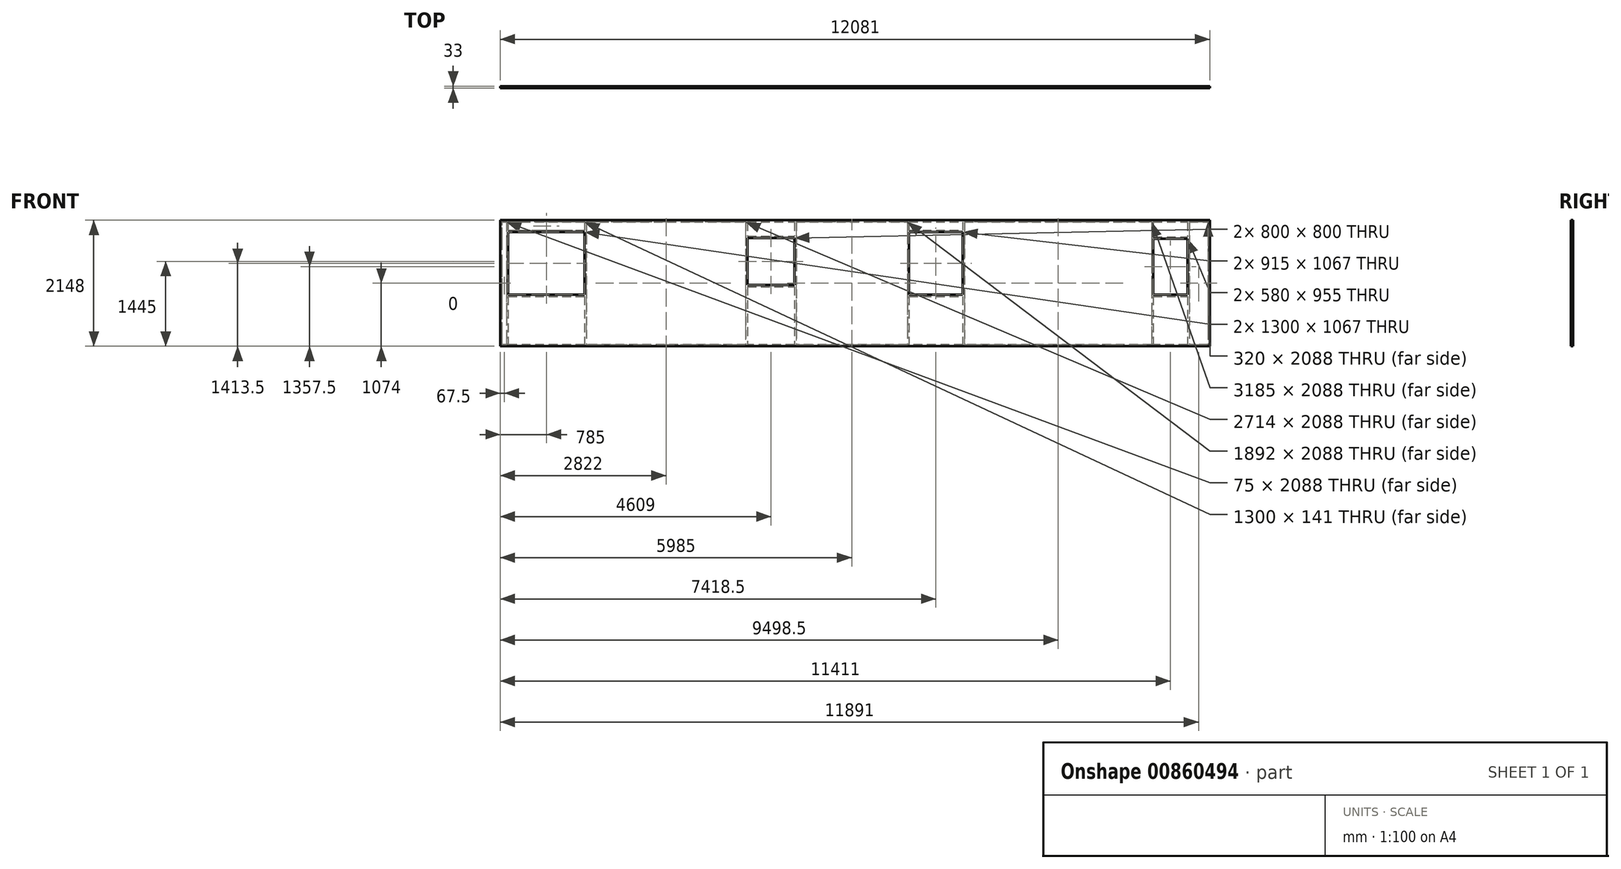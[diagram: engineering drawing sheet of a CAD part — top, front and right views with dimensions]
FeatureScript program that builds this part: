
annotation { "Feature Type Name" : "Feature", "Feature Type Description" : "" }
export const myFeature = defineFeature(function(context is Context, id is Id, definition is map)
    precondition{}
    {
        {
            var Q0;
            Q0=qCreatedBy(makeId("Front.planeOp"),FACE);
            var sketch = newSketch(context, id + "F0", { "sketchPlane" : qUnion([Q0])});
            skLineSegment(sketch, "E0", {"start": v(0, 0) * mm, "end": v(-6025.5, 0) * mm});
            skLineSegment(sketch, "E1", {"start": v(-6025.5, 0) * mm, "end": v(-6025.5, 2088) * mm});
            skLineSegment(sketch, "E2", {"start": v(-6025.5, 2088) * mm, "end": v(6025.5, 2088) * mm});
            skLineSegment(sketch, "E3", {"start": v(6025.5, 2088) * mm, "end": v(6025.5, 0) * mm});
            skLineSegment(sketch, "E4", {"start": v(6025.5, 0) * mm, "end": v(0, 0) * mm});
            skLineSegment(sketch, "E5", {"start": v(5995.5, 2088) * mm, "end": v(5995.5, 0) * mm});
            skLineSegment(sketch, "E6", {"start": v(6025.5, 2118) * mm, "end": v(1575.5, 2118) * mm});
            skLineSegment(sketch, "E7", {"start": v(6025.5, 2118) * mm, "end": v(6025.5, 2088) * mm});
            skLineSegment(sketch, "E8", {"start": v(1575.5, 2118) * mm, "end": v(1575.5, 2088) * mm});
            skLineSegment(sketch, "E9", {"start": v(1575.5, 2118) * mm, "end": v(-3474.5, 2118) * mm});
            skLineSegment(sketch, "E10", {"start": v(-3474.5, 2118) * mm, "end": v(-3474.5, 2088) * mm});
            skLineSegment(sketch, "E11", {"start": v(-3474.5, 2118) * mm, "end": v(-6055.5, 2118) * mm});
            skLineSegment(sketch, "E12", {"start": v(-6055.5, 2118) * mm, "end": v(-6055.5, -30) * mm});
            skLineSegment(sketch, "E13", {"start": v(-6055.5, -30) * mm, "end": v(6025.5, -30) * mm});
            skLineSegment(sketch, "E14", {"start": v(6025.5, -30) * mm, "end": v(6025.5, 0) * mm});
            skLineSegment(sketch, "E15", {"start": v(5675.5, 2088) * mm, "end": v(5675.5, 0) * mm});
            skLineSegment(sketch, "E16", {"start": v(5065.5, 2088) * mm, "end": v(5065.5, 0) * mm});
            skLineSegment(sketch, "E17", {"start": v(5645.5, 2088) * mm, "end": v(5645.5, 0) * mm});
            skLineSegment(sketch, "E18", {"start": v(5035.5, 2088) * mm, "end": v(5035.5, 0) * mm});
            skLineSegment(sketch, "E19", {"start": v(5065.5, 850) * mm, "end": v(5645.5, 850) * mm});
            skLineSegment(sketch, "E20", {"start": v(5065.5, 820) * mm, "end": v(5645.5, 820) * mm});
            skLineSegment(sketch, "E21", {"start": v(5065.5, 1805) * mm, "end": v(5645.5, 1805) * mm});
            skLineSegment(sketch, "E22", {"start": v(5065.5, 1835) * mm, "end": v(5645.5, 1835) * mm});
            skLineSegment(sketch, "E23", {"start": v(1850.5, 2088) * mm, "end": v(1850.5, 0) * mm});
            skLineSegment(sketch, "E24", {"start": v(1820.5, 2088) * mm, "end": v(1820.5, 0) * mm});
            skLineSegment(sketch, "E25", {"start": v(875.5, 2088) * mm, "end": v(875.5, 0) * mm});
            skLineSegment(sketch, "E26", {"start": v(905.5, 2088) * mm, "end": v(905.5, 0) * mm});
            skLineSegment(sketch, "E27", {"start": v(905.5, 850) * mm, "end": v(1820.5, 850) * mm});
            skLineSegment(sketch, "E28", {"start": v(905.5, 820) * mm, "end": v(1820.5, 820) * mm});
            skLineSegment(sketch, "E29", {"start": v(905.5, 1947) * mm, "end": v(1820.5, 1947) * mm});
            skLineSegment(sketch, "E30", {"start": v(905.5, 1917) * mm, "end": v(1820.5, 1917) * mm});
            skLineSegment(sketch, "E31", {"start": v(-1016.5, 2088) * mm, "end": v(-1016.5, 0) * mm});
            skLineSegment(sketch, "E32", {"start": v(-1046.5, 2088) * mm, "end": v(-1046.5, 0) * mm});
            skLineSegment(sketch, "E33", {"start": v(-1846.5, 2088) * mm, "end": v(-1846.5, 0) * mm});
            skLineSegment(sketch, "E34", {"start": v(-1876.5, 2088) * mm, "end": v(-1876.5, 0) * mm});
            skLineSegment(sketch, "E35", {"start": v(-1846.5, 1015) * mm, "end": v(-1046.5, 1015) * mm});
            skLineSegment(sketch, "E36", {"start": v(-1846.5, 985) * mm, "end": v(-1046.5, 985) * mm});
            skLineSegment(sketch, "E37", {"start": v(-1846.5, 1845) * mm, "end": v(-1046.5, 1845) * mm});
            skLineSegment(sketch, "E38", {"start": v(-1846.5, 1815) * mm, "end": v(-1046.5, 1815) * mm});
            skLineSegment(sketch, "E39", {"start": v(-5950.5, 2088) * mm, "end": v(-5950.5, 0) * mm});
            skLineSegment(sketch, "E40", {"start": v(-5920.5, 2088) * mm, "end": v(-5920.5, 0) * mm});
            skLineSegment(sketch, "E41", {"start": v(-4620.5, 2088) * mm, "end": v(-4620.5, 0) * mm});
            skLineSegment(sketch, "E42", {"start": v(-4590.5, 2088) * mm, "end": v(-4590.5, 0) * mm});
            skLineSegment(sketch, "E43", {"start": v(-5920.5, 1947) * mm, "end": v(-4620.5, 1947) * mm});
            skLineSegment(sketch, "E44", {"start": v(-5920.5, 1917) * mm, "end": v(-4620.5, 1917) * mm});
            skLineSegment(sketch, "E45", {"start": v(-5920.5, 850) * mm, "end": v(-4620.5, 850) * mm});
            skLineSegment(sketch, "E46", {"start": v(-5920.5, 820) * mm, "end": v(-4620.5, 820) * mm});
            skSolve(sketch);
        }
        {
            var Q0;
            Q0 = qSketchRegion(id + "F0", true);
            var Q1;
            {var subQ0=sQuery(id+"F0.wireOp",EDGE,"E43");Q1=makeQuery(id+"F0.imprint","IMPRINT",FACE,{"disambiguationData":[TD([[makeQuery(id+"F0.imprint","IMPRINT",EDGE,{"derivedFrom":subQ0}),-1.0]])]});}
            var Q2;
            {var subQ5=sQuery(id+"F0.wireOp",EDGE,"E42");Q2=makeQuery(id+"F0.imprint","IMPRINT",FACE,{"disambiguationData":[TD([[makeQuery(id+"F0.imprint","IMPRINT",EDGE,{"derivedFrom":subQ5}),-1.0]])]});}
            var Q3;
            {var subQ0=sQuery(id+"F0.wireOp",EDGE,"E45");Q3=makeQuery(id+"F0.imprint","IMPRINT",FACE,{"disambiguationData":[TD([[makeQuery(id+"F0.imprint","IMPRINT",EDGE,{"derivedFrom":subQ0}),-1.0]])]});}
            var Q4;
            {var subQ4=sQuery(id+"F0.wireOp",EDGE,"E39");Q4=makeQuery(id+"F0.imprint","IMPRINT",FACE,{"disambiguationData":[TD([[makeQuery(id+"F0.imprint","IMPRINT",EDGE,{"derivedFrom":subQ4}),1.0]])]});}
            var Q5;
            {var subQ5=sQuery(id+"F0.wireOp",EDGE,"E34");Q5=makeQuery(id+"F0.imprint","IMPRINT",FACE,{"disambiguationData":[TD([[makeQuery(id+"F0.imprint","IMPRINT",EDGE,{"derivedFrom":subQ5}),1.0]])]});}
            var Q6;
            {var subQ0=sQuery(id+"F0.wireOp",EDGE,"E37");Q6=makeQuery(id+"F0.imprint","IMPRINT",FACE,{"disambiguationData":[TD([[makeQuery(id+"F0.imprint","IMPRINT",EDGE,{"derivedFrom":subQ0}),-1.0]])]});}
            var Q7;
            {var subQ0=sQuery(id+"F0.wireOp",EDGE,"E35");Q7=makeQuery(id+"F0.imprint","IMPRINT",FACE,{"disambiguationData":[TD([[makeQuery(id+"F0.imprint","IMPRINT",EDGE,{"derivedFrom":subQ0}),-1.0]])]});}
            var Q8;
            {var subQ4=sQuery(id+"F0.wireOp",EDGE,"E31");Q8=makeQuery(id+"F0.imprint","IMPRINT",FACE,{"disambiguationData":[TD([[makeQuery(id+"F0.imprint","IMPRINT",EDGE,{"derivedFrom":subQ4}),-1.0]])]});}
            var Q9;
            {var subQ0=sQuery(id+"F0.wireOp",EDGE,"E25");Q9=makeQuery(id+"F0.imprint","IMPRINT",FACE,{"disambiguationData":[TD([[makeQuery(id+"F0.imprint","IMPRINT",EDGE,{"derivedFrom":subQ0}),1.0]])]});}
            var Q10;
            {var subQ0=sQuery(id+"F0.wireOp",EDGE,"E29");Q10=makeQuery(id+"F0.imprint","IMPRINT",FACE,{"disambiguationData":[TD([[makeQuery(id+"F0.imprint","IMPRINT",EDGE,{"derivedFrom":subQ0}),-1.0]])]});}
            var Q11;
            {var subQ0=sQuery(id+"F0.wireOp",EDGE,"E27");Q11=makeQuery(id+"F0.imprint","IMPRINT",FACE,{"disambiguationData":[TD([[makeQuery(id+"F0.imprint","IMPRINT",EDGE,{"derivedFrom":subQ0}),-1.0]])]});}
            var Q12;
            {var subQ0=sQuery(id+"F0.wireOp",EDGE,"E23");Q12=makeQuery(id+"F0.imprint","IMPRINT",FACE,{"disambiguationData":[TD([[makeQuery(id+"F0.imprint","IMPRINT",EDGE,{"derivedFrom":subQ0}),-1.0]])]});}
            var Q13;
            {var subQ7=sQuery(id+"F0.wireOp",EDGE,"E18");Q13=makeQuery(id+"F0.imprint","IMPRINT",FACE,{"disambiguationData":[TD([[makeQuery(id+"F0.imprint","IMPRINT",EDGE,{"derivedFrom":subQ7}),1.0]])]});}
            var Q14;
            {var subQ0=sQuery(id+"F0.wireOp",EDGE,"E21");Q14=makeQuery(id+"F0.imprint","IMPRINT",FACE,{"disambiguationData":[TD([[makeQuery(id+"F0.imprint","IMPRINT",EDGE,{"derivedFrom":subQ0}),1.0]])]});}
            var Q15;
            {var subQ0=sQuery(id+"F0.wireOp",EDGE,"E19");Q15=makeQuery(id+"F0.imprint","IMPRINT",FACE,{"disambiguationData":[TD([[makeQuery(id+"F0.imprint","IMPRINT",EDGE,{"derivedFrom":subQ0}),-1.0]])]});}
            var Q16;
            {var subQ0=sQuery(id+"F0.wireOp",EDGE,"E15");Q16=makeQuery(id+"F0.imprint","IMPRINT",FACE,{"disambiguationData":[TD([[makeQuery(id+"F0.imprint","IMPRINT",EDGE,{"derivedFrom":subQ0}),-1.0]])]});}
            extrude(context, id + "F1", {"entities" : qUnion([Q0, Q1, Q2, Q3, Q4, Q5, Q6, Q7, Q8, Q9, Q10, Q11, Q12, Q13, Q14, Q15, Q16]), "depth" : 30 * mm, "offsetDistance" : 25 * mm});
        }
        {
            var Q0;
            Q0=makeQuery(id+"F1.opExtrude","CAP_FACE",FACE,{"disambiguationData":[OSD([sQuery(id+"F0.wireOp",EDGE,"E0"),sQuery(id+"F0.wireOp",EDGE,"E1"),sQuery(id+"F0.wireOp",EDGE,"E2"),sQuery(id+"F0.wireOp",EDGE,"E3"),sQuery(id+"F0.wireOp",EDGE,"E4"),sQuery(id+"F0.wireOp",EDGE,"E5"),sQuery(id+"F0.wireOp",EDGE,"E6"),sQuery(id+"F0.wireOp",EDGE,"E7"),sQuery(id+"F0.wireOp",EDGE,"E9"),sQuery(id+"F0.wireOp",EDGE,"E11"),sQuery(id+"F0.wireOp",EDGE,"E12"),sQuery(id+"F0.wireOp",EDGE,"E13"),sQuery(id+"F0.wireOp",EDGE,"E14"),sQuery(id+"F0.wireOp",EDGE,"E15"),sQuery(id+"F0.wireOp",EDGE,"E16"),sQuery(id+"F0.wireOp",EDGE,"E17"),sQuery(id+"F0.wireOp",EDGE,"E18"),sQuery(id+"F0.wireOp",EDGE,"E19"),sQuery(id+"F0.wireOp",EDGE,"E20"),sQuery(id+"F0.wireOp",EDGE,"E21"),sQuery(id+"F0.wireOp",EDGE,"E22"),sQuery(id+"F0.wireOp",EDGE,"E23"),sQuery(id+"F0.wireOp",EDGE,"E24"),sQuery(id+"F0.wireOp",EDGE,"E25"),sQuery(id+"F0.wireOp",EDGE,"E26"),sQuery(id+"F0.wireOp",EDGE,"E27"),sQuery(id+"F0.wireOp",EDGE,"E28"),sQuery(id+"F0.wireOp",EDGE,"E29"),sQuery(id+"F0.wireOp",EDGE,"E30"),sQuery(id+"F0.wireOp",EDGE,"E31"),sQuery(id+"F0.wireOp",EDGE,"E32"),sQuery(id+"F0.wireOp",EDGE,"E33"),sQuery(id+"F0.wireOp",EDGE,"E34"),sQuery(id+"F0.wireOp",EDGE,"E35"),sQuery(id+"F0.wireOp",EDGE,"E36"),sQuery(id+"F0.wireOp",EDGE,"E37"),sQuery(id+"F0.wireOp",EDGE,"E38"),sQuery(id+"F0.wireOp",EDGE,"E39"),sQuery(id+"F0.wireOp",EDGE,"E40"),sQuery(id+"F0.wireOp",EDGE,"E41"),sQuery(id+"F0.wireOp",EDGE,"E42"),sQuery(id+"F0.wireOp",EDGE,"E43"),sQuery(id+"F0.wireOp",EDGE,"E44"),sQuery(id+"F0.wireOp",EDGE,"E45"),sQuery(id+"F0.wireOp",EDGE,"E46")])],"isStart":false});
            var sketch = newSketch(context, id + "F2", { "sketchPlane" : qUnion([Q0])});
            skLineSegment(sketch, "E47.bottom", {"start": v(-6055.5, -30) * mm, "end": v(6025.5, -30) * mm});
            skLineSegment(sketch, "E47.top", {"start": v(-6055.5, 2118) * mm, "end": v(6025.5, 2118) * mm});
            skLineSegment(sketch, "E47.left", {"start": v(-6055.5, -30) * mm, "end": v(-6055.5, 2118) * mm});
            skLineSegment(sketch, "E47.right", {"start": v(6025.5, -30) * mm, "end": v(6025.5, 2118) * mm});
            skLineSegment(sketch, "E48.bottom", {"start": v(5065.5, 1805) * mm, "end": v(5645.5, 1805) * mm});
            skLineSegment(sketch, "E48.top", {"start": v(5065.5, 850) * mm, "end": v(5645.5, 850) * mm});
            skLineSegment(sketch, "E48.left", {"start": v(5065.5, 1805) * mm, "end": v(5065.5, 850) * mm});
            skLineSegment(sketch, "E48.right", {"start": v(5645.5, 1805) * mm, "end": v(5645.5, 850) * mm});
            skLineSegment(sketch, "E49.bottom", {"start": v(905.5, 1917) * mm, "end": v(1820.5, 1917) * mm});
            skLineSegment(sketch, "E49.top", {"start": v(905.5, 850) * mm, "end": v(1820.5, 850) * mm});
            skLineSegment(sketch, "E49.left", {"start": v(905.5, 1917) * mm, "end": v(905.5, 850) * mm});
            skLineSegment(sketch, "E49.right", {"start": v(1820.5, 1917) * mm, "end": v(1820.5, 850) * mm});
            skLineSegment(sketch, "E50.bottom", {"start": v(-1846.5, 1815) * mm, "end": v(-1046.5, 1815) * mm});
            skLineSegment(sketch, "E50.top", {"start": v(-1846.5, 1015) * mm, "end": v(-1046.5, 1015) * mm});
            skLineSegment(sketch, "E50.left", {"start": v(-1846.5, 1815) * mm, "end": v(-1846.5, 1015) * mm});
            skLineSegment(sketch, "E50.right", {"start": v(-1046.5, 1815) * mm, "end": v(-1046.5, 1015) * mm});
            skLineSegment(sketch, "E51.bottom", {"start": v(-5920.5, 1917) * mm, "end": v(-4620.5, 1917) * mm});
            skLineSegment(sketch, "E51.top", {"start": v(-5920.5, 850) * mm, "end": v(-4620.5, 850) * mm});
            skLineSegment(sketch, "E51.left", {"start": v(-5920.5, 1917) * mm, "end": v(-5920.5, 850) * mm});
            skLineSegment(sketch, "E51.right", {"start": v(-4620.5, 1917) * mm, "end": v(-4620.5, 850) * mm});
            skSolve(sketch);
        }
        {
            var Q0;
            Q0 = qSketchRegion(id + "F2", true);
            extrude(context, id + "F3", {"entities" : qUnion([Q0]), "depth" : 3 * mm, "offsetDistance" : 25 * mm});
        }
    });
